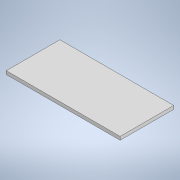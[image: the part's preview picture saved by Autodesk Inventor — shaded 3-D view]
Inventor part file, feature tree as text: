
AUTODESK INVENTOR PART (.ipt)
format: ipt  version: 2022 (Build 260153000, 153)  size: 90,624 bytes
history: native  units: mm
features: extrude x1, sketch x1
ambient origin geometry x8: Origin, YZ Plane, XZ Plane, XY Plane, X Axis, Y Axis, Z Axis, Center Point
bodies: Solid1 (feature_tree)
feature tree (2):
  extrude  "Extrusion1"  Depth=160.0mm
  sketch  "Sketch1"  dims[d0=340.0mm d1=160.0mm d2=10.0mm d3=0.0mm]
